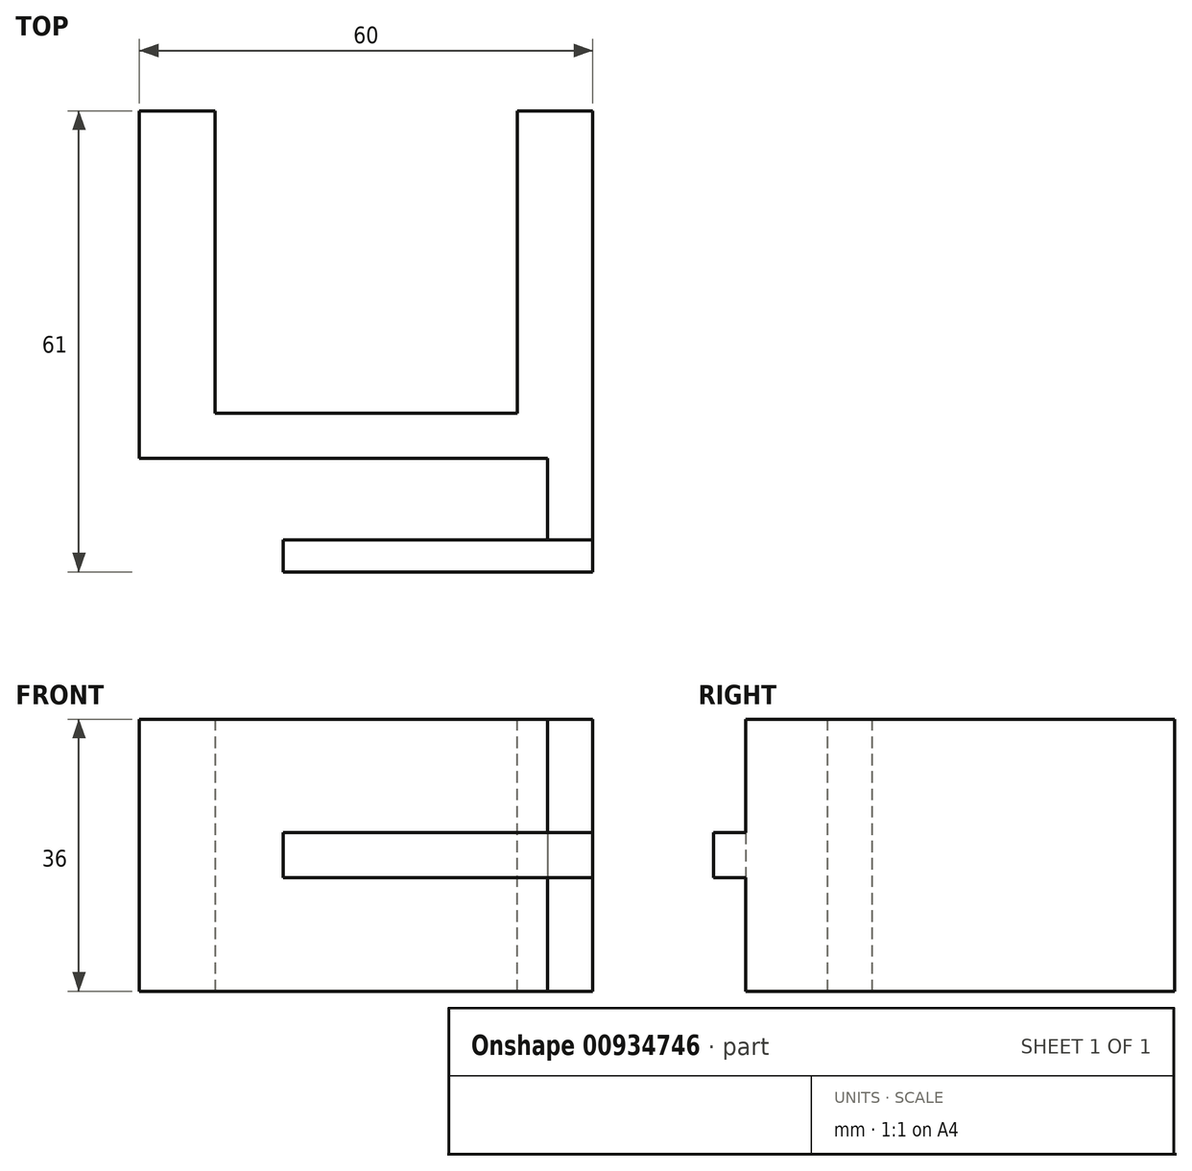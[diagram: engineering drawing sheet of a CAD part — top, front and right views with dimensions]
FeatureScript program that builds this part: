
annotation { "Feature Type Name" : "Feature", "Feature Type Description" : "" }
export const myFeature = defineFeature(function(context is Context, id is Id, definition is map)
    precondition{}
    {
        {
            var Q0;
            Q0=qCreatedBy(makeId("Top.planeOp"),FACE);
            var sketch = newSketch(context, id + "F0", { "sketchPlane" : qUnion([Q0])});
            skLineSegment(sketch, "E0.bottom", {"start": v(-8.34, 0) * mm, "end": v(31.66, 0) * mm});
            skLineSegment(sketch, "E0.top", {"start": v(-8.34, -60) * mm, "end": v(31.66, -60) * mm});
            skLineSegment(sketch, "E0.left", {"start": v(-8.34, 0) * mm, "end": v(-8.34, -60) * mm});
            skLineSegment(sketch, "E0.right", {"start": v(31.66, 0) * mm, "end": v(31.66, -60) * mm});
            skLineSegment(sketch, "E1.bottom", {"start": v(-8.34, -12.1) * mm, "end": v(-8.34, -12.1) * mm});
            skLineSegment(sketch, "E1.top", {"start": v(-8.34, -60) * mm, "end": v(-8.34, -60) * mm});
            skLineSegment(sketch, "E1.left", {"start": v(-8.34, -12.1) * mm, "end": v(-8.34, -60) * mm});
            skLineSegment(sketch, "E1.right", {"start": v(-8.34, -12.1) * mm, "end": v(-8.34, -60) * mm});
            skLineSegment(sketch, "E2.bottom", {"start": v(-8.34, -60) * mm, "end": v(-18.34, -60) * mm});
            skLineSegment(sketch, "E2.top", {"start": v(-8.34, 0) * mm, "end": v(-18.34, 0) * mm});
            skLineSegment(sketch, "E2.left", {"start": v(-8.34, -60) * mm, "end": v(-8.34, 0) * mm});
            skLineSegment(sketch, "E2.right", {"start": v(-18.34, -60) * mm, "end": v(-18.34, 0) * mm});
            skLineSegment(sketch, "E3.bottom", {"start": v(31.66, -60) * mm, "end": v(41.66, -60) * mm});
            skLineSegment(sketch, "E3.top", {"start": v(31.66, 0) * mm, "end": v(41.66, 0) * mm});
            skLineSegment(sketch, "E3.left", {"start": v(31.66, -60) * mm, "end": v(31.66, 0) * mm});
            skLineSegment(sketch, "E3.right", {"start": v(41.66, -60) * mm, "end": v(41.66, 0) * mm});
            skSolve(sketch);
        }
        {
            var Q0;
            Q0 = qSketchRegion(id + "F0", true);
            var Q1;
            {var subQ3=sQuery(id+"F0.wireOp",EDGE,"E0.bottom");Q1=makeQuery(id+"F0.imprint","IMPRINT",FACE,{"disambiguationData":[TD([[makeQuery(id+"F0.imprint","IMPRINT",EDGE,{"derivedFrom":subQ3}),-1.0]])]});}
            extrude(context, id + "F1", {"entities" : qUnion([Q0, Q1]), "depth" : 6 * mm, "offsetDistance" : 25 * mm});
        }
        {
            var Q0;
            Q0=makeQuery(id+"F1.opExtrude","CAP_FACE",FACE,{"disambiguationData":[OSD([sQuery(id+"F0.wireOp",EDGE,"E0.bottom"),sQuery(id+"F0.wireOp",EDGE,"E0.top"),sQuery(id+"F0.wireOp",EDGE,"E2.bottom"),sQuery(id+"F0.wireOp",EDGE,"E2.top"),sQuery(id+"F0.wireOp",EDGE,"E2.right"),sQuery(id+"F0.wireOp",EDGE,"E3.bottom"),sQuery(id+"F0.wireOp",EDGE,"E3.top"),sQuery(id+"F0.wireOp",EDGE,"E3.right")])],"isStart":false});
            var sketch = newSketch(context, id + "F2", { "sketchPlane" : qUnion([Q0])});
            skLineSegment(sketch, "E4.bottom", {"start": v(-18.34, -60) * mm, "end": v(-8.34, -60) * mm});
            skLineSegment(sketch, "E4.top", {"start": v(-18.34, 0) * mm, "end": v(-8.34, 0) * mm});
            skLineSegment(sketch, "E4.left", {"start": v(-18.34, -60) * mm, "end": v(-18.34, 0) * mm});
            skLineSegment(sketch, "E4.right", {"start": v(-8.34, -60) * mm, "end": v(-8.34, 0) * mm});
            skLineSegment(sketch, "E5.bottom", {"start": v(41.66, 0) * mm, "end": v(31.66, 0) * mm});
            skLineSegment(sketch, "E5.top", {"start": v(41.66, -60) * mm, "end": v(31.66, -60) * mm});
            skLineSegment(sketch, "E5.left", {"start": v(41.66, 0) * mm, "end": v(41.66, -60) * mm});
            skLineSegment(sketch, "E5.right", {"start": v(31.66, 0) * mm, "end": v(31.66, -60) * mm});
            skSolve(sketch);
        }
        {
            var Q0;
            Q0 = qSketchRegion(id + "F2", true);
            extrude(context, id + "F3", {"entities" : qUnion([Q0]), "operationType" : NewBodyOperationType.ADD, "depth" : 40 * mm, "offsetDistance" : 25 * mm});
        }
        {
            var Q0;
            Q0=makeQuery(id+"F1.opExtrude","CAP_FACE",FACE,{"disambiguationData":[OSD([sQuery(id+"F0.wireOp",EDGE,"E0.bottom"),sQuery(id+"F0.wireOp",EDGE,"E0.top"),sQuery(id+"F0.wireOp",EDGE,"E2.bottom"),sQuery(id+"F0.wireOp",EDGE,"E2.top"),sQuery(id+"F0.wireOp",EDGE,"E2.right"),sQuery(id+"F0.wireOp",EDGE,"E3.bottom"),sQuery(id+"F0.wireOp",EDGE,"E3.top"),sQuery(id+"F0.wireOp",EDGE,"E3.right")])],"isStart":true});
            var sketch = newSketch(context, id + "F4", { "sketchPlane" : qUnion([Q0])});
            skLineSegment(sketch, "E6.bottom", {"start": v(41.66, 48) * mm, "end": v(35.66, 48) * mm});
            skLineSegment(sketch, "E6.top", {"start": v(41.66, 12) * mm, "end": v(35.66, 12) * mm});
            skLineSegment(sketch, "E6.left", {"start": v(41.66, 48) * mm, "end": v(41.66, 12) * mm});
            skLineSegment(sketch, "E6.right", {"start": v(35.66, 48) * mm, "end": v(35.66, 12) * mm});
            skSolve(sketch);
        }
        {
            var Q0;
            Q0 = qSketchRegion(id + "F4", true);
            extrude(context, id + "F5", {"entities" : qUnion([Q0]), "operationType" : NewBodyOperationType.ADD, "depth" : 15 * mm, "offsetDistance" : 25 * mm});
        }
        {
            var Q0;
            Q0=makeQuery(id+"F5.opExtrude","SWEPT_FACE",FACE,{"disambiguationData":[OSD([sQuery(id+"F4.wireOp",EDGE,"E6.right")])]});
            var sketch = newSketch(context, id + "F6", { "sketchPlane" : qUnion([Q0])});
            skLineSegment(sketch, "E7.bottom", {"start": v(48, -15) * mm, "end": v(12, -15) * mm});
            skLineSegment(sketch, "E7.top", {"start": v(48, -10.76) * mm, "end": v(12, -10.76) * mm});
            skLineSegment(sketch, "E7.left", {"start": v(48, -15) * mm, "end": v(48, -10.76) * mm});
            skLineSegment(sketch, "E7.right", {"start": v(12, -15) * mm, "end": v(12, -10.76) * mm});
            skSolve(sketch);
        }
        {
            var Q0;
            Q0 = qSketchRegion(id + "F6", true);
            extrude(context, id + "F7", {"entities" : qUnion([Q0]), "operationType" : NewBodyOperationType.ADD, "depth" : 35 * mm, "offsetDistance" : 25 * mm});
        }
        {
            var Q0;
            Q0=makeQuery(id+"F1.opExtrude","SWEPT_BODY",BODY,{"disambiguationData":[OSD([sQuery(id+"F0.wireOp",EDGE,"E0.bottom"),sQuery(id+"F0.wireOp",EDGE,"E0.top"),sQuery(id+"F0.wireOp",EDGE,"E2.bottom"),sQuery(id+"F0.wireOp",EDGE,"E2.top"),sQuery(id+"F0.wireOp",EDGE,"E2.right"),sQuery(id+"F0.wireOp",EDGE,"E3.bottom"),sQuery(id+"F0.wireOp",EDGE,"E3.top"),sQuery(id+"F0.wireOp",EDGE,"E3.right")])]});
            var Q1;
            Q1=makeQuery(id+"F1.opExtrude","CAP_EDGE",EDGE,{"disambiguationData":[OSD([sQuery(id+"F0.wireOp",EDGE,"E0.top"),sQuery(id+"F0.wireOp",EDGE,"E2.bottom"),sQuery(id+"F0.wireOp",EDGE,"E3.bottom")])],"isStart":true});
            transform(context, id + "F8", {"entities" : qUnion([Q0]), "transformType" : TransformType.ROTATION, "transformAxis" : qUnion([Q1]), "angle" : 90 * degree, "makeCopy" : false});
        }
        {
            var Q0;
            Q0=makeQuery(id+"F7.boolean.opBoolean","MERGE",FACE,{"derivedFrom":[makeQuery(id+"F5.opExtrude","SWEPT_FACE",FACE,{"disambiguationData":[OSD([sQuery(id+"F4.wireOp",EDGE,"E6.bottom")])]}),makeQuery(id+"F7.opExtrude","SWEPT_FACE",FACE,{"disambiguationData":[OSD([sQuery(id+"F6.wireOp",EDGE,"E7.left")])]})]});
            var sketch = newSketch(context, id + "F9", { "sketchPlane" : qUnion([Q0])});
            skLineSegment(sketch, "E8.bottom", {"start": v(41.66, -75) * mm, "end": v(-33.74, -75) * mm});
            skLineSegment(sketch, "E8.top", {"start": v(41.66, 8.18) * mm, "end": v(-33.74, 8.18) * mm});
            skLineSegment(sketch, "E8.left", {"start": v(41.66, -75) * mm, "end": v(41.66, 8.18) * mm});
            skLineSegment(sketch, "E8.right", {"start": v(-33.74, -75) * mm, "end": v(-33.74, 8.18) * mm});
            skSolve(sketch);
        }
        {
            var Q0;
            Q0 = qSketchRegion(id + "F9", true);
            extrude(context, id + "F10", {"entities" : qUnion([Q0]), "operationType" : NewBodyOperationType.REMOVE, "depth" : 132.6 * mm, "offsetDistance" : 25 * mm});
        }
        {
            var Q0;
            Q0=makeQuery(id+"F7.boolean.opBoolean","MERGE",FACE,{"derivedFrom":[makeQuery(id+"F5.opExtrude","SWEPT_FACE",FACE,{"disambiguationData":[OSD([sQuery(id+"F4.wireOp",EDGE,"E6.top")])]}),makeQuery(id+"F7.opExtrude","SWEPT_FACE",FACE,{"disambiguationData":[OSD([sQuery(id+"F6.wireOp",EDGE,"E7.right")])]})]});
            var sketch = newSketch(context, id + "F11", { "sketchPlane" : qUnion([Q0])});
            skLineSegment(sketch, "E9.bottom", {"start": v(41.66, 75) * mm, "end": v(-33.66, 75) * mm});
            skLineSegment(sketch, "E9.top", {"start": v(41.66, -69.62) * mm, "end": v(-33.66, -69.62) * mm});
            skLineSegment(sketch, "E9.left", {"start": v(41.66, 75) * mm, "end": v(41.66, -69.62) * mm});
            skLineSegment(sketch, "E9.right", {"start": v(-33.66, 75) * mm, "end": v(-33.66, -69.62) * mm});
            skSolve(sketch);
        }
        {
            var Q0;
            {var subQ2=sQuery(id+"F4.wireOp",EDGE,"E6.top");var subQ6=makeQuery(id+"F5.opExtrude","CAP_EDGE",EDGE,{"disambiguationData":[OSD([subQ2])],"isStart":true});Q0=makeQuery(id+"F11.imprint","IMPRINT",FACE,{"disambiguationData":[TD([[makeQuery(id+"F11.imprint","IMPRINT",EDGE,{"derivedFrom":subQ6}),-1.0]])]});}
            var Q1;
            {var subQ3=sQuery(id+"F11.wireOp",EDGE,"E9.top");Q1=makeQuery(id+"F11.imprint","IMPRINT",FACE,{"disambiguationData":[TD([[makeQuery(id+"F11.imprint","IMPRINT",EDGE,{"derivedFrom":subQ3}),-1.0]])]});}
            extrude(context, id + "F12", {"entities" : qUnion([Q0, Q1]), "operationType" : NewBodyOperationType.REMOVE, "depth" : 173.4 * mm, "offsetDistance" : 25 * mm});
        }
        {
            var Q0;
            Q0=makeQuery(id+"F10.boolean.opBoolean","MERGE",FACE,{"derivedFrom":[makeQuery(id+"F7.boolean.opBoolean","MERGE",FACE,{"derivedFrom":[makeQuery(id+"F5.opExtrude","SWEPT_FACE",FACE,{"disambiguationData":[OSD([sQuery(id+"F4.wireOp",EDGE,"E6.bottom")])]}),makeQuery(id+"F7.opExtrude","SWEPT_FACE",FACE,{"disambiguationData":[OSD([sQuery(id+"F6.wireOp",EDGE,"E7.left")])]})]})],"fromTools":[makeQuery(id+"F10.opExtrude","CAP_FACE",FACE,{"disambiguationData":[OSD([sQuery(id+"F9.wireOp",EDGE,"E8.bottom"),sQuery(id+"F9.wireOp",EDGE,"E8.top"),sQuery(id+"F9.wireOp",EDGE,"E8.left"),sQuery(id+"F9.wireOp",EDGE,"E8.right")])],"isStart":true})]});
            var sketch = newSketch(context, id + "F13", { "sketchPlane" : qUnion([Q0])});
            skLineSegment(sketch, "E10.bottom", {"start": v(0.66, -75) * mm, "end": v(41.66, -75) * mm});
            skLineSegment(sketch, "E10.top", {"start": v(0.66, -70.76) * mm, "end": v(41.66, -70.76) * mm});
            skLineSegment(sketch, "E10.left", {"start": v(0.66, -75) * mm, "end": v(0.66, -70.76) * mm});
            skLineSegment(sketch, "E10.right", {"start": v(41.66, -75) * mm, "end": v(41.66, -70.76) * mm});
            skSolve(sketch);
        }
        {
            var Q0;
            Q0 = qSketchRegion(id + "F13", true);
            extrude(context, id + "F14", {"entities" : qUnion([Q0]), "operationType" : NewBodyOperationType.REMOVE, "oppositeDirection" : true, "depth" : 15 * mm, "offsetDistance" : 25 * mm});
        }
        {
            var Q0;
            Q0=makeQuery(id+"F12.boolean.opBoolean","MERGE",FACE,{"derivedFrom":[makeQuery(id+"F7.boolean.opBoolean","MERGE",FACE,{"derivedFrom":[makeQuery(id+"F5.opExtrude","SWEPT_FACE",FACE,{"disambiguationData":[OSD([sQuery(id+"F4.wireOp",EDGE,"E6.top")])]}),makeQuery(id+"F7.opExtrude","SWEPT_FACE",FACE,{"disambiguationData":[OSD([sQuery(id+"F6.wireOp",EDGE,"E7.right")])]})]})],"fromTools":[makeQuery(id+"F12.opExtrude","CAP_FACE",FACE,{"disambiguationData":[OSD([sQuery(id+"F11.wireOp",EDGE,"E9.bottom"),sQuery(id+"F11.wireOp",EDGE,"E9.top"),sQuery(id+"F11.wireOp",EDGE,"E9.left"),sQuery(id+"F11.wireOp",EDGE,"E9.right")])],"isStart":true})]});
            var sketch = newSketch(context, id + "F15", { "sketchPlane" : qUnion([Q0])});
            skLineSegment(sketch, "E11.bottom", {"start": v(41.66, 75) * mm, "end": v(0.66, 75) * mm});
            skLineSegment(sketch, "E11.top", {"start": v(41.66, 70.76) * mm, "end": v(0.66, 70.76) * mm});
            skLineSegment(sketch, "E11.left", {"start": v(41.66, 75) * mm, "end": v(41.66, 70.76) * mm});
            skLineSegment(sketch, "E11.right", {"start": v(0.66, 75) * mm, "end": v(0.66, 70.76) * mm});
            skSolve(sketch);
        }
        {
            var Q0;
            Q0 = qSketchRegion(id + "F15", true);
            extrude(context, id + "F16", {"entities" : qUnion([Q0]), "operationType" : NewBodyOperationType.REMOVE, "oppositeDirection" : true, "depth" : 15 * mm, "offsetDistance" : 25 * mm});
        }
    });
